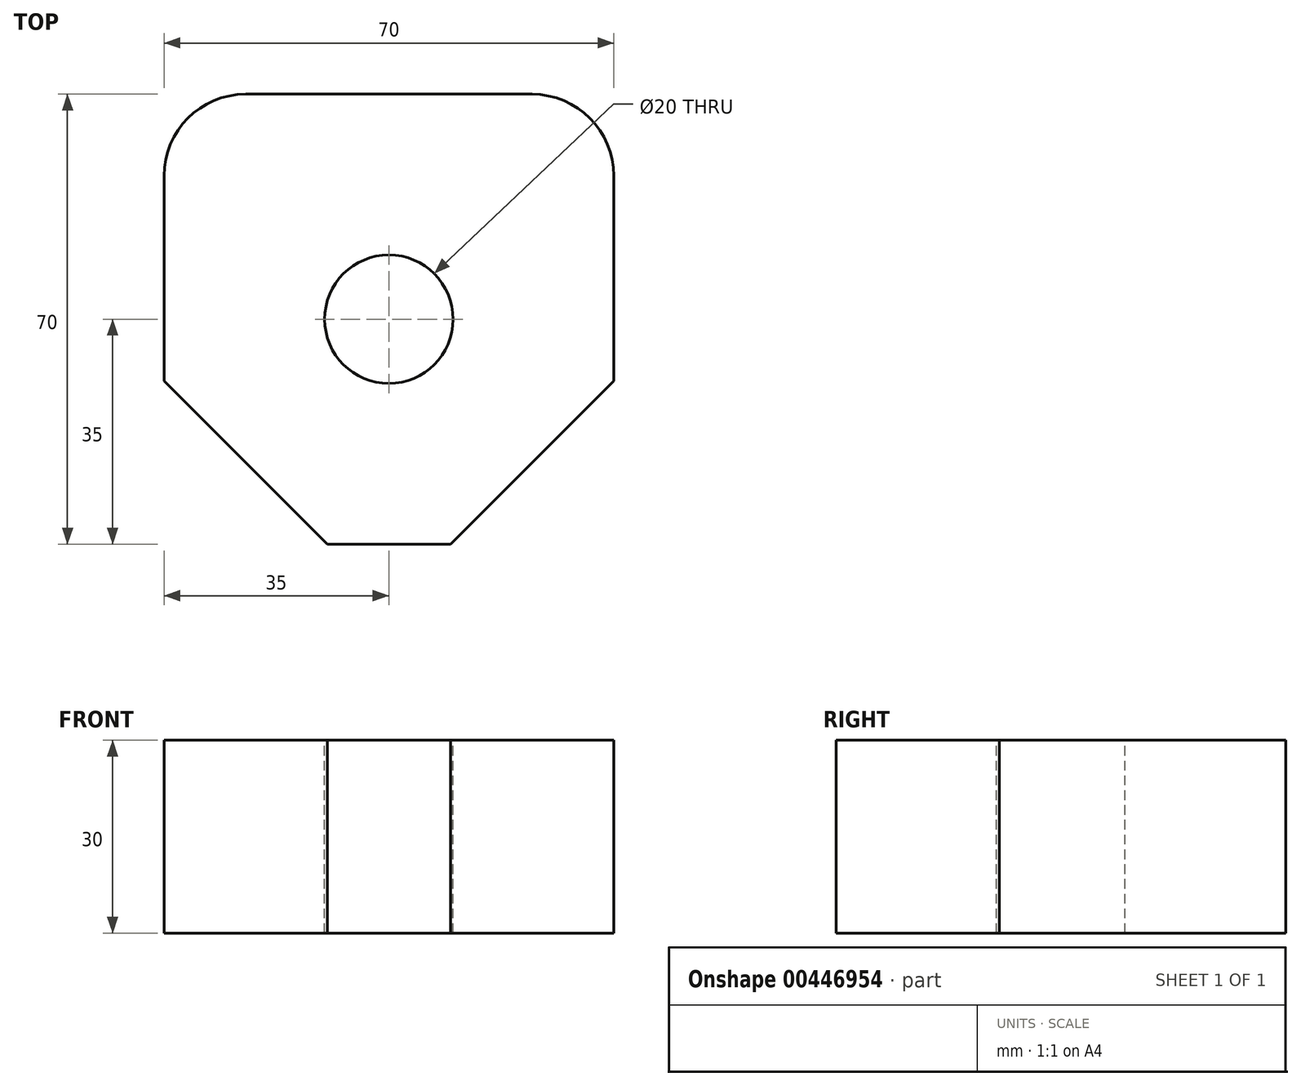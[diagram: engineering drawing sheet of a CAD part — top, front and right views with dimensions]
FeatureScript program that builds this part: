
annotation { "Feature Type Name" : "Feature", "Feature Type Description" : "" }
export const myFeature = defineFeature(function(context is Context, id is Id, definition is map)
    precondition{}
    {
        {
            var Q0;
            Q0=qCreatedBy(makeId("Front.planeOp"),FACE);
            var sketch = newSketch(context, id + "F0", { "sketchPlane" : qUnion([Q0])});
            skLineSegment(sketch, "E0.bottom", {"start": v(35, 15) * mm, "end": v(-35, 15) * mm});
            skLineSegment(sketch, "E0.top", {"start": v(35, -15) * mm, "end": v(-35, -15) * mm});
            skLineSegment(sketch, "E0.left", {"start": v(35, 15) * mm, "end": v(35, -15) * mm});
            skLineSegment(sketch, "E0.right", {"start": v(-35, 15) * mm, "end": v(-35, -15) * mm});
            skPoint(sketch, "E0.middle", {"position": v(0, 0) * mm});
            skSolve(sketch);
        }
        {
            var Q0;
            Q0 = qSketchRegion(id + "F0", true);
            extrude(context, id + "F1", {"entities" : qUnion([Q0]), "depth" : 70 * mm});
        }
        {
            var Q0;
            Q0=makeQuery(id+"F1.opExtrude","SWEPT_FACE",FACE,{"disambiguationData":[OSD([sQuery(id+"F0.wireOp",EDGE,"E0.bottom")])]});
            var sketch = newSketch(context, id + "F2", { "sketchPlane" : qUnion([Q0])});
            skCircle(sketch, "E1", {"center": v(0, -35) * mm, "radius": 10 * mm});
            skPoint(sketch, "E1.centerSnap0", {"position": v(-35, -35) * mm});
            skSolve(sketch);
        }
        {
            var Q0;
            Q0 = qSketchRegion(id + "F2", true);
            extrude(context, id + "F3", {"entities" : qUnion([Q0]), "operationType" : NewBodyOperationType.REMOVE, "endBound" : BoundingType.THROUGH_ALL, "oppositeDirection" : true, "depth" : 25.4 * mm});
        }
        {
            var Q0;
            Q0=makeQuery(id+"F1.opExtrude","CAP_EDGE",EDGE,{"disambiguationData":[OSD([sQuery(id+"F0.wireOp",EDGE,"E0.right")])],"isStart":true});
            var Q1;
            Q1=makeQuery(id+"F1.opExtrude","CAP_EDGE",EDGE,{"disambiguationData":[OSD([sQuery(id+"F0.wireOp",EDGE,"E0.left")])],"isStart":true});
            fillet(context, id + "F4", {"entities" : qUnion([Q0, Q1]), "radius" : 12.7 * mm, "tangentPropagation" : true, "allowEdgeOverflow" : false});
        }
        {
            var Q0;
            Q0=makeQuery(id+"F1.opExtrude","CAP_EDGE",EDGE,{"disambiguationData":[OSD([sQuery(id+"F0.wireOp",EDGE,"E0.right")])],"isStart":false});
            var Q1;
            Q1=makeQuery(id+"F1.opExtrude","CAP_EDGE",EDGE,{"disambiguationData":[OSD([sQuery(id+"F0.wireOp",EDGE,"E0.left")])],"isStart":false});
            chamfer(context, id + "F5", {"entities" : qUnion([Q0, Q1]), "width" : 25.4 * mm, "tangentPropagation" : true});
        }
    });
